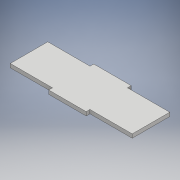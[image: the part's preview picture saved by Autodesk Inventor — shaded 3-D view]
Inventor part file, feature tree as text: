
AUTODESK INVENTOR PART (.ipt)
format: ipt  version: 2018 (Build 220112000, 112)  size: 101,888 bytes
history: native  units: mm
features: extrude x1, sketch x1
ambient origin geometry x8: Origin, YZ Plane, XZ Plane, XY Plane, X Axis, Y Axis, Z Axis, Center Point
bodies: Solid1 (feature_tree)
feature tree (2):
  extrude  "Extrusion1"  Depth=40.0mm
  sketch  "Sketch1"  dims[d0=40.0mm d1=40.0mm d2=130.0mm d3=4.0mm d4=0.0mm]
